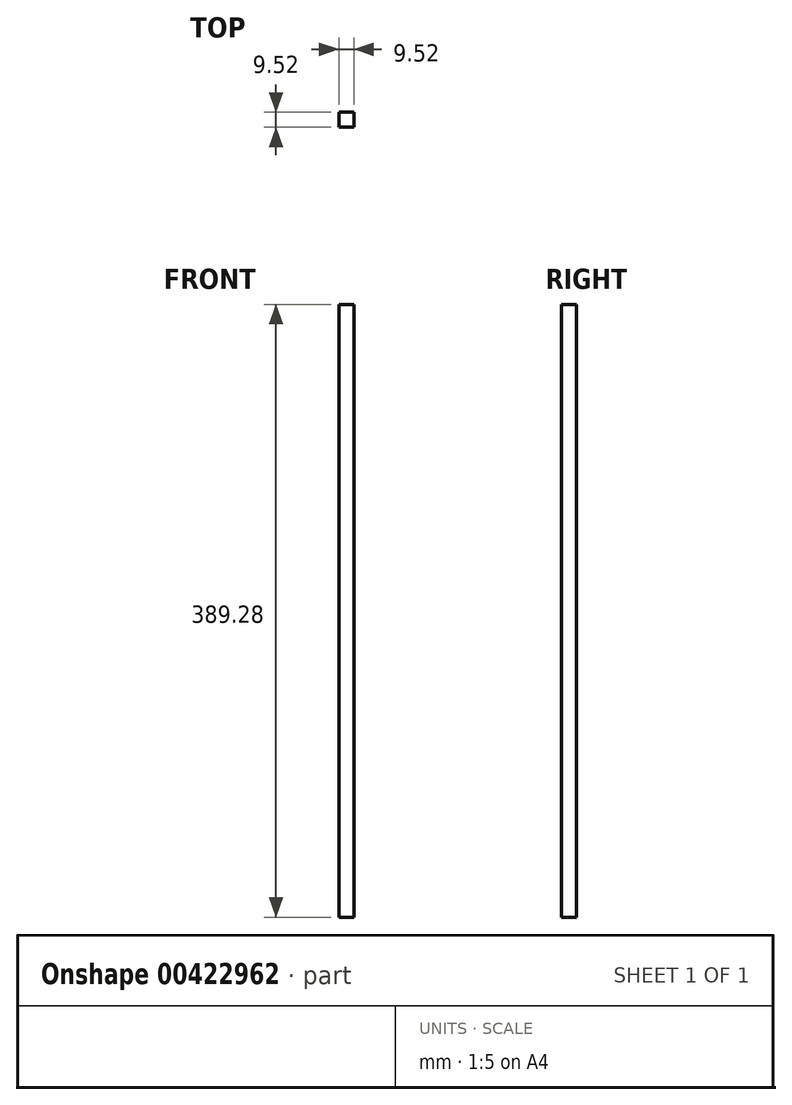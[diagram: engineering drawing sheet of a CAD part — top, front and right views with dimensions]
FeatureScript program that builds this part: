
annotation { "Feature Type Name" : "Feature", "Feature Type Description" : "" }
export const myFeature = defineFeature(function(context is Context, id is Id, definition is map)
    precondition{}
    {
        {
            var Q0;
            Q0=qCreatedBy(makeId("Top.planeOp"),FACE);
            var sketch = newSketch(context, id + "F0", { "sketchPlane" : qUnion([Q0])});
            skPoint(sketch, "E0.middle", {"position": v(0, 0) * mm});
            skLineSegment(sketch, "E1.bottom", {"start": v(4.76, 4.76) * mm, "end": v(-4.76, 4.76) * mm});
            skLineSegment(sketch, "E1.top", {"start": v(4.76, -4.76) * mm, "end": v(-4.76, -4.76) * mm});
            skLineSegment(sketch, "E1.left", {"start": v(4.76, 4.76) * mm, "end": v(4.76, -4.76) * mm});
            skLineSegment(sketch, "E1.right", {"start": v(-4.76, 4.76) * mm, "end": v(-4.76, -4.76) * mm});
            skSolve(sketch);
        }
        {
            var Q0;
            Q0 = qSketchRegion(id + "F0", true);
            extrude(context, id + "F1", {"entities" : qUnion([Q0]), "depth" : 389.28 * mm, "offsetDistance" : 25.4 * mm});
        }
    });
